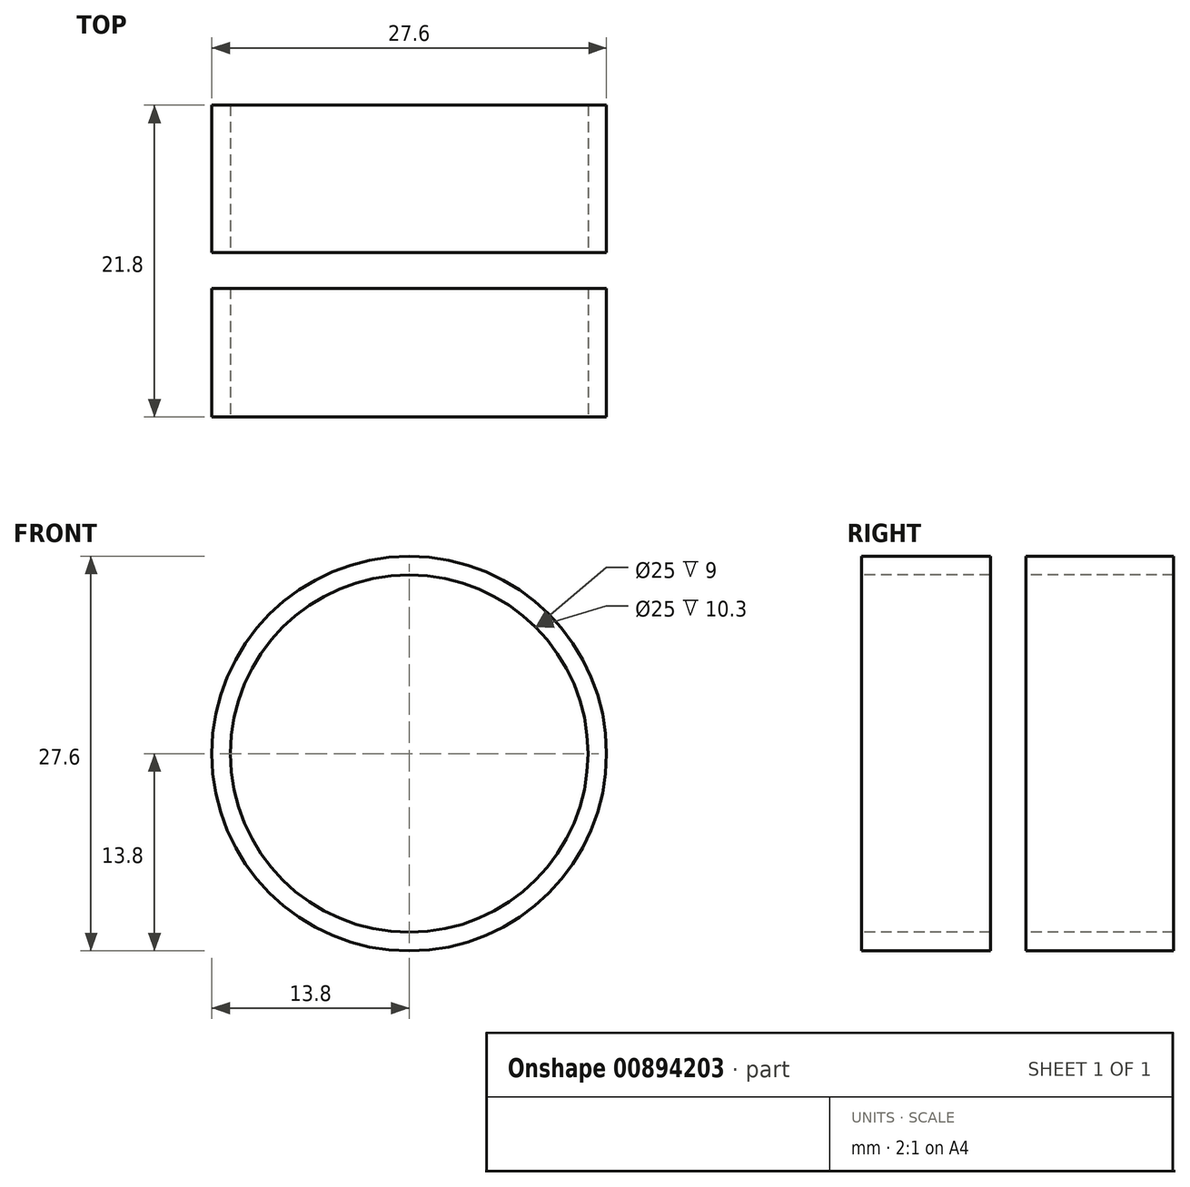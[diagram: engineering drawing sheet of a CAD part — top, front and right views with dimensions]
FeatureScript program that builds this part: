
annotation { "Feature Type Name" : "Feature", "Feature Type Description" : "" }
export const myFeature = defineFeature(function(context is Context, id is Id, definition is map)
    precondition{}
    {
        {
            var Q0;
            Q0=qCreatedBy(makeId("Right.planeOp"),FACE);
            var sketch = newSketch(context, id + "F0", { "sketchPlane" : qUnion([Q0])});
            skLineSegment(sketch, "E0", {"start": v(0, 0) * mm, "end": v(0, 12.5) * mm, "construction": true});
            skLineSegment(sketch, "E1", {"start": v(0, 12.5) * mm, "end": v(0, 13.8) * mm});
            skLineSegment(sketch, "E2", {"start": v(0, 13.8) * mm, "end": v(9, 13.8) * mm});
            skLineSegment(sketch, "E3", {"start": v(9, 13.8) * mm, "end": v(9, 12.5) * mm});
            skLineSegment(sketch, "E4", {"start": v(9, 12.5) * mm, "end": v(0, 12.5) * mm});
            skLineSegment(sketch, "E5", {"start": v(11.5, 12.5) * mm, "end": v(11.5, 13.8) * mm});
            skLineSegment(sketch, "E6", {"start": v(11.5, 13.8) * mm, "end": v(21.8, 13.8) * mm});
            skLineSegment(sketch, "E7", {"start": v(21.8, 13.8) * mm, "end": v(21.8, 12.5) * mm});
            skLineSegment(sketch, "E8", {"start": v(21.8, 12.5) * mm, "end": v(11.5, 12.5) * mm});
            skLineSegment(sketch, "E9", {"start": v(0, 0) * mm, "end": v(21.8, 0) * mm});
            skSolve(sketch);
        }
        {
            var Q0;
            Q0 = qSketchRegion(id + "F0", true);
            var Q1;
            Q1=sQuery(id+"F0.wireOp",EDGE,"E9");
            revolve(context, id + "F1", {"surfaceOperationType" : NewSurfaceOperationType.NEW, "entities" : qUnion([Q0]), "axis" : qUnion([Q1]), "revolveType" : RevolveType.FULL});
        }
    });
